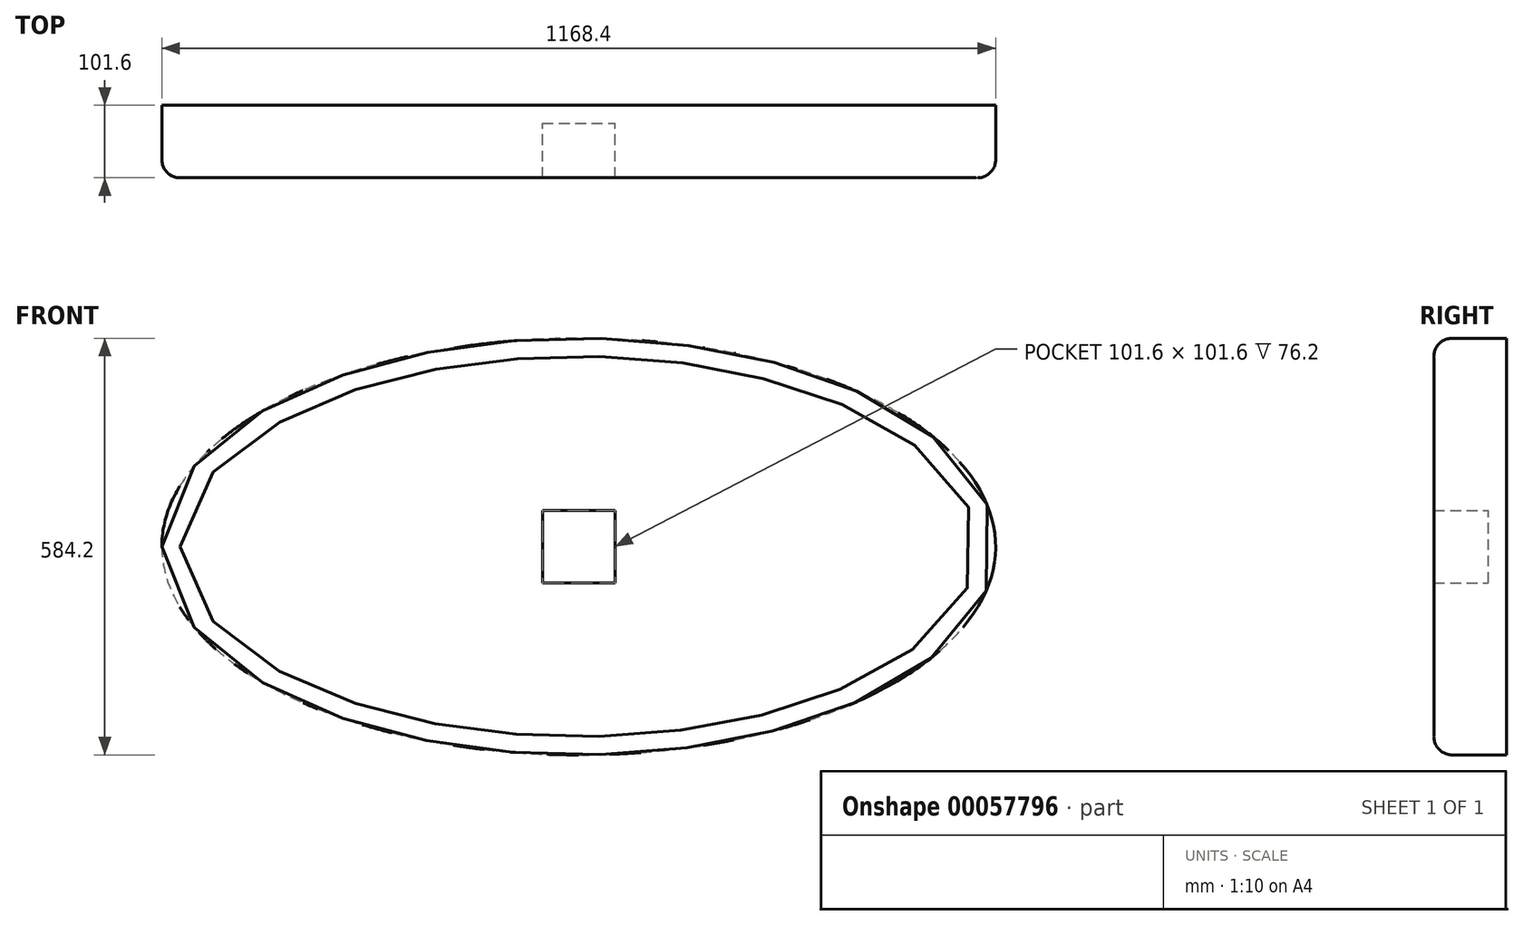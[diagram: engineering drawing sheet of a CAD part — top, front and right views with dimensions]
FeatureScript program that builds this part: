
annotation { "Feature Type Name" : "Feature", "Feature Type Description" : "" }
export const myFeature = defineFeature(function(context is Context, id is Id, definition is map)
    precondition{}
    {
        {
            var Q0;
            Q0=qCreatedBy(makeId("Front.planeOp"),FACE);
            var sketch = newSketch(context, id + "F0", { "sketchPlane" : qUnion([Q0])});
            skEllipse(sketch, "E0", {"center": v(0, 0) * mm, "majorRadius": 584.2 * mm, "minorRadius": 292.1 * mm, "majorAxis": v(-1, 0)});
            skLineSegment(sketch, "E1.rect.bottom", {"start": v(-50.8, -50.8) * mm, "end": v(50.8, -50.8) * mm});
            skLineSegment(sketch, "E1.rect.top", {"start": v(-50.8, 50.8) * mm, "end": v(50.8, 50.8) * mm});
            skLineSegment(sketch, "E1.rect.left", {"start": v(-50.8, -50.8) * mm, "end": v(-50.8, 50.8) * mm});
            skLineSegment(sketch, "E1.rect.right", {"start": v(50.8, -50.8) * mm, "end": v(50.8, 50.8) * mm});
            skSolve(sketch);
        }
        {
            var Q0;
            Q0=makeQuery(id+"F0.imprint","IMPRINT",FACE,{"disambiguationData":[TD([[makeQuery(id+"F0.imprint","IMPRINT",EDGE,{"derivedFrom":sQuery(id+"F0.wireOp",EDGE,"E0")}),1.0]])]});
            extrude(context, id + "F1", {"entities" : qUnion([Q0]), "depth" : 101.6 * mm});
        }
        {
            var Q0;
            Q0=makeQuery(id+"F0.imprint","IMPRINT",FACE,{"disambiguationData":[TD([[makeQuery(id+"F0.imprint","IMPRINT",EDGE,{"derivedFrom":sQuery(id+"F0.wireOp",EDGE,"E1.rect.bottom")}),1.0]])]});
            extrude(context, id + "F2", {"entities" : qUnion([Q0]), "operationType" : NewBodyOperationType.ADD, "depth" : 25.4 * mm});
        }
        {
            var Q0;
            Q0=makeQuery(id+"F1.opExtrude","CAP_EDGE",EDGE,{"disambiguationData":[OSD([sQuery(id+"F0.wireOp",EDGE,"E0")])],"isStart":false});
            fillet(context, id + "F3", {"entities" : qUnion([Q0]), "radius" : 25.4 * mm, "tangentPropagation" : true, "allowEdgeOverflow" : false});
        }
    });
